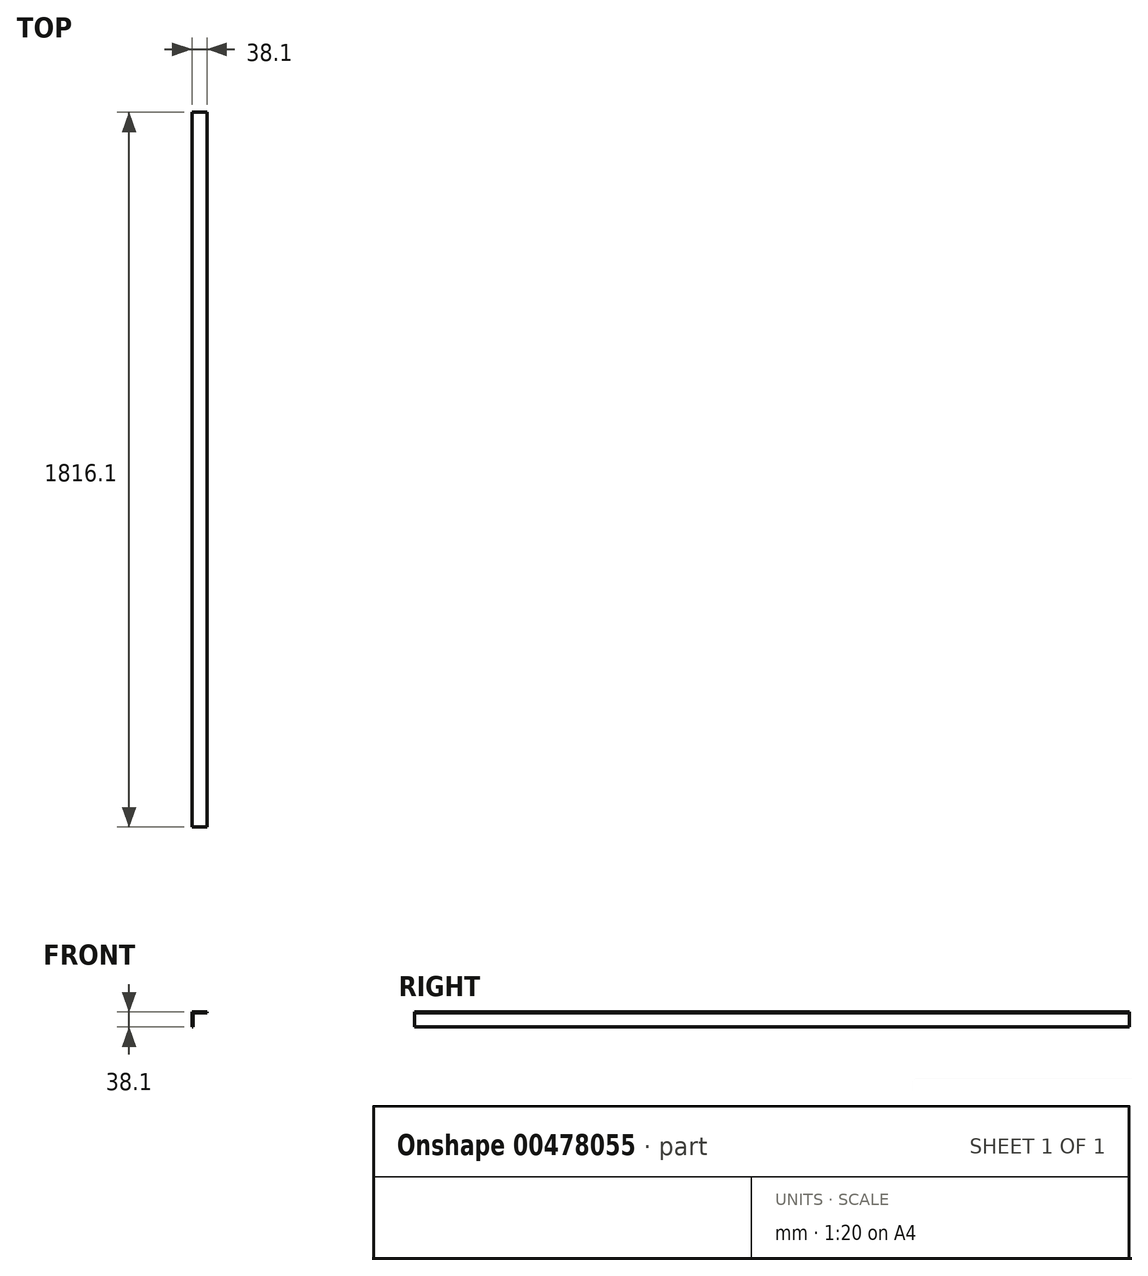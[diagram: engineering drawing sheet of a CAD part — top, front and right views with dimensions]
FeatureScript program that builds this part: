
annotation { "Feature Type Name" : "Feature", "Feature Type Description" : "" }
export const myFeature = defineFeature(function(context is Context, id is Id, definition is map)
    precondition{}
    {
        {
            var Q0;
            Q0=qCreatedBy(makeId("Front.planeOp"),FACE);
            var sketch = newSketch(context, id + "F0", { "sketchPlane" : qUnion([Q0])});
            skLineSegment(sketch, "E0.bottom", {"start": v(-51.34, 19.1) * mm, "end": v(-48.67, 19.1) * mm});
            skLineSegment(sketch, "E0.top", {"start": v(-51.34, 57.2) * mm, "end": v(-48.67, 57.2) * mm});
            skLineSegment(sketch, "E0.left", {"start": v(-51.34, 19.1) * mm, "end": v(-51.34, 57.2) * mm});
            skLineSegment(sketch, "E0.right", {"start": v(-48.67, 19.1) * mm, "end": v(-48.67, 54.54) * mm});
            skLineSegment(sketch, "E1.bottom", {"start": v(-48.67, 57.2) * mm, "end": v(-13.24, 57.2) * mm});
            skLineSegment(sketch, "E1.top", {"start": v(-48.67, 54.54) * mm, "end": v(-13.24, 54.54) * mm});
            skLineSegment(sketch, "E1.right", {"start": v(-13.24, 57.2) * mm, "end": v(-13.24, 54.54) * mm});
            skSolve(sketch);
        }
        {
            var Q0;
            Q0=makeQuery(id+"F0.imprint","IMPRINT",FACE,{"disambiguationData":[TD([[makeQuery(id+"F0.imprint","IMPRINT",EDGE,{"derivedFrom":sQuery(id+"F0.wireOp",EDGE,"E0.bottom")}),1.0]])]});
            extrude(context, id + "F1", {"entities" : qUnion([Q0]), "depth" : 1816.1 * mm});
        }
    });
